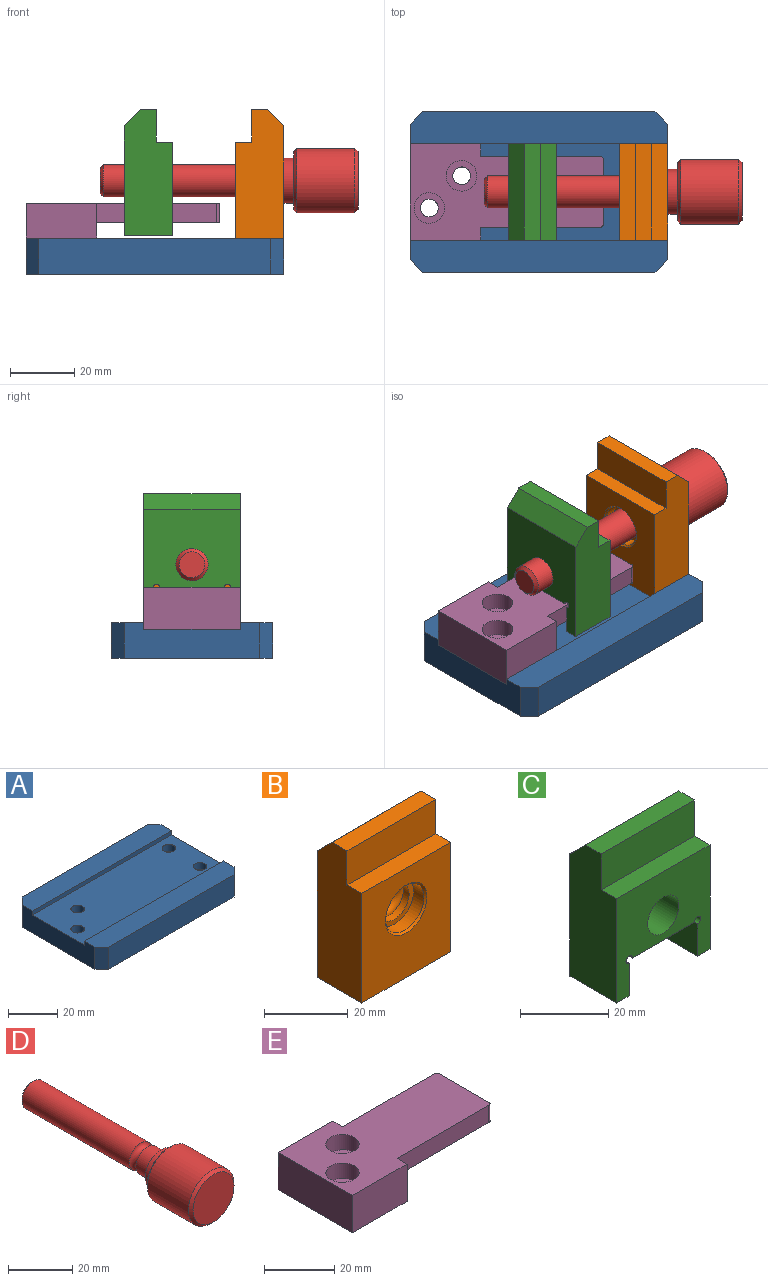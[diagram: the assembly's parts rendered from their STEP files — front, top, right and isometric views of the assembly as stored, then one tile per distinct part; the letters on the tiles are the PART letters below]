
ASSEMBLY  parts=5 mates=10
PART A: 22 faces, bbox 80x50x11 mm
  f0: plane 80x30mm, normal (0,0,1), area 2305mm2, adj f3,f5,f12,f13,f18,f19,f20,f21
  f1: plane 80x50mm, normal (0,0,-1), area 3778.7mm2, adj f3,f4,f5,f6,f8,f9,f10,f11
  f2: plane 80x10mm, normal (0,0,1), area 784mm2, adj f3,f5,f6,f10,f11,f13
  f3: plane 42x11mm, normal (1,0,0), area 402mm2, adj f0,f1,f2,f7,f9,f11,f12,f13
  f4: plane 72x11mm, normal (0,1,0), area 792mm2, adj f1,f7,f8,f9
  f5: plane 42x11mm, normal (-1,0,0), area 402mm2, adj f0,f1,f2,f7,f8,f10,f12,f13
  f6: plane 72x11mm, normal (0,-1,0), area 792mm2, adj f1,f2,f10,f11
  f7: plane 80x10mm, normal (0,0,1), area 784mm2, adj f3,f4,f5,f8,f9,f12
  f8: plane 11x4mm, normal (-0.71,0.71,0), area 62.2mm2, adj f1,f4,f5,f7
  f9: plane 11x4mm, normal (0.71,0.71,0), area 62.2mm2, adj f1,f3,f4,f7
  f10: plane 11x4mm, normal (-0.71,-0.71,0), area 62.2mm2, adj f1,f2,f5,f6
  f11: plane 11x4mm, normal (0.71,-0.71,0), area 62.2mm2, adj f1,f2,f3,f6
  f12: plane 80x2mm, normal (0,-1,0), area 160mm2, adj f0,f3,f5,f7
  f13: plane 80x2mm, normal (0,1,0), area 160mm2, adj f0,f2,f3,f5
  f14: cylinder r=4.75mm len=9.5mm, axis (0,0,-1), area 161.2mm2, adj f1,f15
  f15: plane 9.5x9.5mm, normal (0,0,-1), area 47.1mm2, adj f14,f19
  f16: cylinder r=4.75mm len=9.5mm, axis (0,0,-1), area 161.2mm2, adj f1,f17
  f17: plane 9.5x9.5mm, normal (0,0,-1), area 47.1mm2, adj f16,f18
  f18: cylinder r=2.75mm len=5.5mm, axis (0,0,1), area 62.2mm2, adj f0,f17
  f19: cylinder r=2.75mm len=5.5mm, axis (0,0,1), area 62.2mm2, adj f0,f15
  f20: cylinder r=2.75mm len=9mm, axis (0,0,1), area 155.5mm2, adj f0,f1
  f21: cylinder r=2.75mm len=9mm, axis (0,0,1), area 155.5mm2, adj f0,f1
PART B: 19 faces, bbox 30x15x42 mm
  f0: plane 32x30mm, normal (0,-1,0), area 806.1mm2, adj f1,f6,f7,f8,f14
  f1: plane 30x15mm, normal (0,0,-1), area 410.7mm2, adj f0,f2,f7,f8,f10,f12
  f2: plane 37x30mm, normal (0,1,0), area 1031.5mm2, adj f1,f3,f7,f8,f15
  f3: plane 30x5mm, normal (0,0.71,0.71), area 212.1mm2, adj f2,f4,f7,f8
  f4: plane 30x5mm, normal (0,0,1), area 150mm2, adj f3,f5,f7,f8
  f5: plane 30x10mm, normal (0,-1,0), area 300mm2, adj f4,f6,f7,f8
  f6: plane 30x5mm, normal (0,0,1), area 150mm2, adj f0,f5,f7,f8
  f7: plane 42x15mm, normal (1,0,0), area 567.5mm2, adj f0,f1,f2,f3,f4,f5,f6
  f8: plane 42x15mm, normal (-1,0,0), area 567.5mm2, adj f0,f1,f2,f3,f4,f5,f6
  f9: cone r=0mm half-angle=59deg, axis (0,0,-1), area 22.9mm2, adj f10
  f10: cylinder r=2.5mm len=12mm, axis (0,0,-1), area 188.5mm2, adj f1,f9
  f11: cone r=0mm half-angle=59deg, axis (0,0,-1), area 22.9mm2, adj f12
  f12: cylinder r=2.5mm len=12mm, axis (0,0,-1), area 188.5mm2, adj f1,f11
  f13: cylinder r=6.5mm len=13mm, axis (0,-1,0), area 142.9mm2, adj f14,f18
  f14: cone r=6.5mm half-angle=45deg, axis (0,-1,0), area 30mm2, adj f0,f13
  f15: cylinder r=5mm len=10mm, axis (0,-1,0), area 188.5mm2, adj f2,f16
  f16: torus R=5mm, axis (0,-1,0), area 119.8mm2, adj f15,f17
  f17: cylinder r=5mm len=10mm, axis (0,-1,0), area 62.8mm2, adj f16,f18
  f18: plane 13x13mm, normal (0,-1,0), area 54.2mm2, adj f13,f17
PART C: 16 faces, bbox 30x15x39 mm
  f0: plane 15x4mm, normal (0,0,-1), area 60mm2, adj f1,f3,f9,f12
  f1: plane 30x29mm, normal (0,-1,0), area 566.7mm2, adj f0,f2,f7,f8,f9,f10,f11,f12
  f2: plane 15x4mm, normal (0,0,-1), area 60mm2, adj f1,f3,f8,f11
  f3: plane 34x30mm, normal (0,1,0), area 716.7mm2, adj f0,f2,f4,f8,f9,f10,f11,f12
  f4: plane 30x5mm, normal (0,0.71,0.71), area 212.1mm2, adj f3,f5,f8,f9
  f5: plane 30x5mm, normal (0,0,1), area 150mm2, adj f4,f6,f8,f9
  f6: plane 30x10mm, normal (0,-1,0), area 300mm2, adj f5,f7,f8,f9
  f7: plane 30x5mm, normal (0,0,1), area 150mm2, adj f1,f6,f8,f9
  f8: plane 39x15mm, normal (1,0,0), area 522.5mm2, adj f1,f2,f3,f4,f5,f6,f7
  f9: plane 39x15mm, normal (-1,0,0), area 522.5mm2, adj f0,f1,f3,f4,f5,f6,f7
  f10: cylinder r=5mm len=15mm, axis (0,1,0), area 471.2mm2, adj f1,f3
  f11: plane 15x9mm, normal (-1,0,0), area 135mm2, adj f1,f2,f3,f13
  f12: plane 15x9mm, normal (1,0,0), area 135mm2, adj f0,f1,f3,f14
  f13: cylinder r=1mm len=15mm, axis (0,1,0), area 70.7mm2, adj f1,f3,f11,f15
  f14: cylinder r=1mm len=15mm, axis (0,1,0), area 70.7mm2, adj f1,f3,f12,f15
  f15: plane 20x15mm, normal (0,0,-1), area 300mm2, adj f1,f3,f13,f14
PART D: 12 faces, bbox 20x80x20 mm
  f0: cone r=9mm half-angle=45deg, axis (0,1,0), area 84.4mm2, adj f1,f11
  f1: plane 18x18mm, normal (0,-1,0), area 254.5mm2, adj f0
  f2: plane 8x8mm, normal (0,1,0), area 50.3mm2, adj f3
  f3: cone r=4mm half-angle=45deg, axis (0,-1,0), area 40mm2, adj f2,f4
  f4: cylinder r=5mm len=47mm, axis (0,-1,0), area 1476.5mm2, adj f3,f5
  f5: torus R=5mm, axis (0,-1,0), area 119.8mm2, adj f4,f6
  f6: cylinder r=5mm len=10mm, axis (0,-1,0), area 188.5mm2, adj f5,f7
  f7: plane 14x14mm, normal (0,1,0), area 75.4mm2, adj f6,f8
  f8: cylinder r=7mm len=14mm, axis (0,-1,0), area 131.9mm2, adj f7,f9
  f9: plane 18x18mm, normal (0,1,0), area 100.5mm2, adj f8,f10
  f10: cone r=10mm half-angle=45deg, axis (0,-1,0), area 84.4mm2, adj f9,f11
  f11: cylinder r=10mm len=20mm, axis (0,-1,0), area 1131mm2, adj f0,f10
PART E: 18 faces, bbox 60x30x13 mm
  f0: plane 22x13mm, normal (0,1,0), area 286mm2, adj f1,f3,f4,f5
  f1: plane 30x13mm, normal (-1,0,0), area 390mm2, adj f0,f2,f4,f5
  f2: plane 22x13mm, normal (0,-1,0), area 286mm2, adj f1,f3,f4,f5
  f3: plane 30x13mm, normal (1,0,0), area 258mm2, adj f0,f2,f4,f5,f6,f7,f8
  f4: plane 30x22mm, normal (0,0,-1), area 612.5mm2, adj f0,f1,f2,f3,f14,f15
  f5: plane 60x30mm, normal (0,0,1), area 1353.8mm2, adj f0,f1,f2,f3,f6,f7,f9,f10
  f6: plane 37x6mm, normal (0,1,0), area 222mm2, adj f3,f5,f8,f17
  f7: plane 37x6mm, normal (0,-1,0), area 222mm2, adj f3,f5,f8,f16
  f8: plane 38x22mm, normal (0,0,-1), area 835.6mm2, adj f3,f6,f7,f9,f16,f17
  f9: plane 20x6mm, normal (1,0,0), area 120mm2, adj f5,f8,f16,f17
  f10: cylinder r=4.75mm len=9.5mm, axis (0,0,1), area 161.2mm2, adj f5,f11
  f11: plane 9.5x9.5mm, normal (0,0,1), area 47.1mm2, adj f10,f14
  f12: cylinder r=4.75mm len=9.5mm, axis (0,0,1), area 161.2mm2, adj f5,f13
  f13: plane 9.5x9.5mm, normal (0,0,1), area 47.1mm2, adj f12,f15
  f14: cylinder r=2.75mm len=7.6mm, axis (0,0,1), area 131.3mm2, adj f4,f11
  f15: cylinder r=2.75mm len=7.6mm, axis (0,0,1), area 131.3mm2, adj f4,f13
  f16: cylinder r=1mm len=6mm, axis (0,0,1), area 9.4mm2, adj f5,f7,f8,f9
  f17: cylinder r=1mm len=6mm, axis (0,0,-1), area 9.4mm2, adj f5,f6,f8,f9
PLACE A t=(0.36,0.83,-5.29)mm fixed
PLACE B rot(axis=(0,0,-1),90deg) t=(32.86,0.83,3.71)mm
PLACE C rot(axis=(0,0,1),90deg) t=(-1.72,0.83,6.71)mm
PLACE D rot(axis=(-0.68,0.68,0.26),150.6deg) t=(63.36,0.83,23.71)mm
PLACE E t=(-39.64,0.83,16.71)mm
MATE planar B.f1 <-> A.f0  axis (0,0,-1) through (32.86,0.83,3.71)mm
MATE slider C.f10 <-> B.f16  axis (1,0,0) through (5.78,0.83,23.71)mm
MATE cylindrical B.f9 <-> A.f14  axis (0,0,-1) through (32.86,9.83,3.71)mm
MATE planar E.f4 <-> A.f0  axis (0,0,-1) through (-28.64,0.83,3.71)mm
MATE cylindrical C.f10 <-> D.f0  axis (-1,0,0) through (-1.72,0.83,23.71)mm
MATE cylindrical E.f10 <-> A.f21  axis (0,0,1) through (-33.64,-4.17,11.31)mm
MATE cylindrical B.f11 <-> A.f16  axis (0,0,-1) through (32.86,-8.17,3.71)mm
MATE cylindrical B.f13 <-> D.f0  axis (-1,0,0) through (40.36,0.83,23.71)mm
MATE cylindrical E.f12 <-> A.f20  axis (0,0,1) through (-23.64,5.83,11.31)mm
MATE planar D.f0 <-> B.f2  axis (-1,0,0) through (40.36,0.83,23.71)mm
